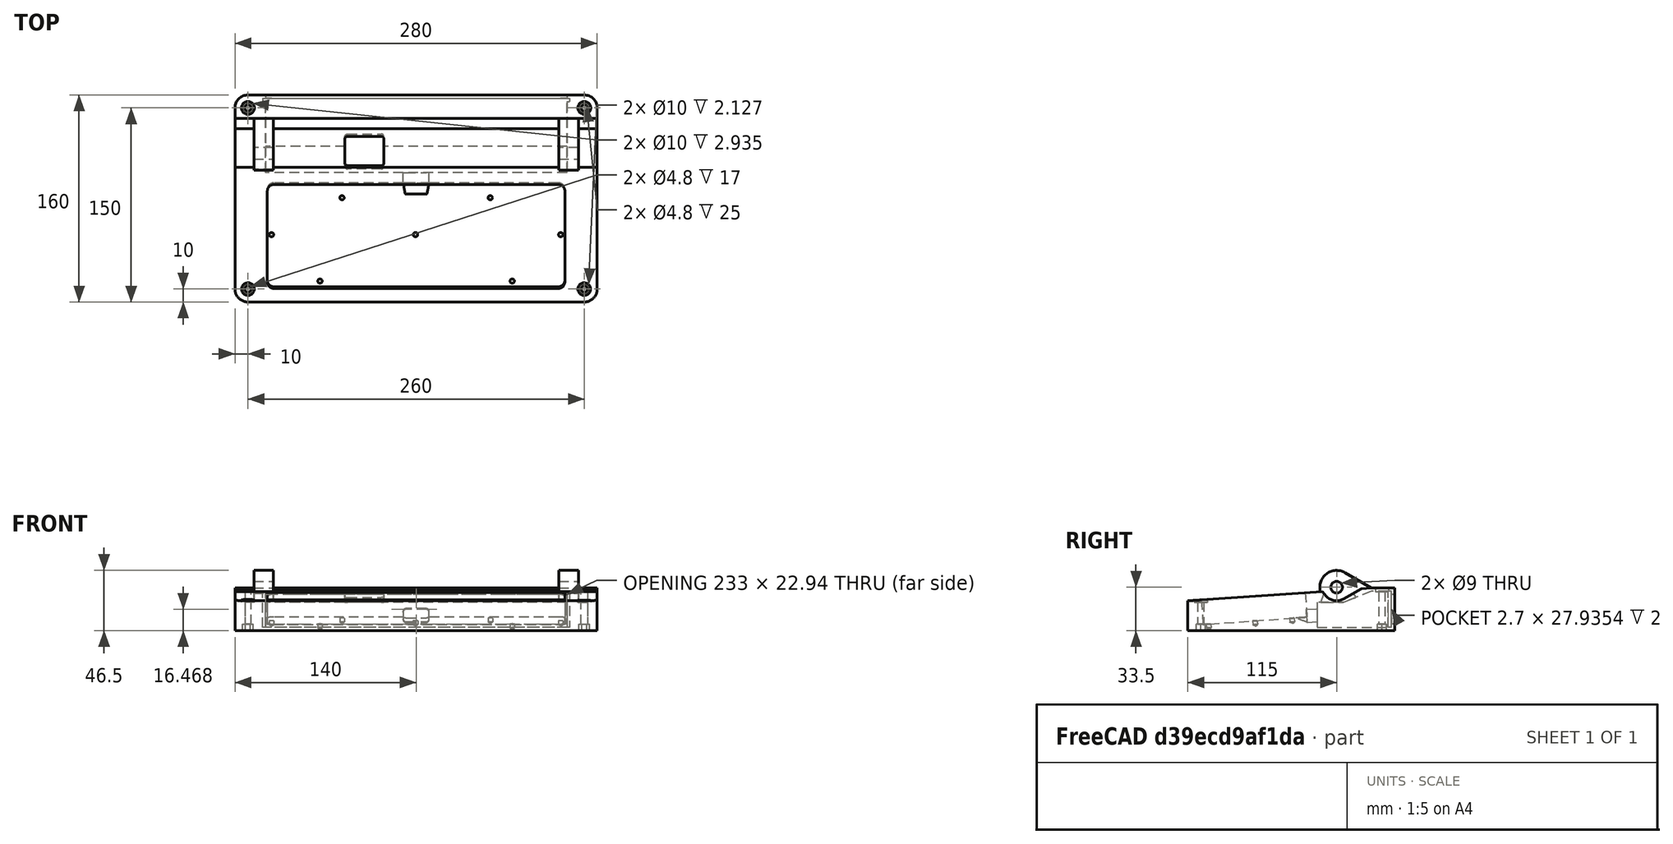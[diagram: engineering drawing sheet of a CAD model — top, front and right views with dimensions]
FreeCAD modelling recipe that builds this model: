
FCSTD DOCUMENT  (FreeCAD 1.0R39285 (Git))
Label: SimpleCheck
License: All rights reserved
LicenseURL: https://en.wikipedia.org/wiki/All_rights_reserved
objects: PartDesign::SubShapeBinder×2, App::Link×1, PartDesign::Boolean×1, PartDesign::Body×1
note: 5 computed .brp shape members not serialized (recipe doc carries the construction recipe); baked Part::Feature solids carry a one-line shape summary decoded from their .brp
EXTERNAL_REF file=Spec.FCStd obj=Spreadsheet
EXTERNAL_REF file=TestAsm.FCStd obj=Assembly
EXTERNAL_REF file=BottomEnclosure_base.FCStd obj=Body

FEATURE [App::Link] Link  label="Vars"
  LinkedObject = -> <external Spec.FCStd>#Spreadsheet
FEATURE [PartDesign::SubShapeBinder] Binder004  label="Top Enclosure"
  BindCopyOnChange = 0
  BindMode = 0
  ClaimChildren = false
  Fuse = false
  MakeFace = true
  OffsetFill = false
  OffsetIntersection = false
  OffsetJoinType = 0
  OffsetOpenResult = false
  PartialLoad = false
  Placement = pos=(0,15,33.5) rot=(1,0,0;1.0472rad)
  Refine = true
  Relative = true
  Support = -> [<external TestAsm.FCStd>#Assembly]
  _Version = 2
  expr: .Placement.Base.z = <<Vars>>.bottom_enclosure_depth + 2.5 + 1
FEATURE [PartDesign::SubShapeBinder] Binder
  BindCopyOnChange = 0
  BindMode = 0
  ClaimChildren = false
  Fuse = false
  MakeFace = true
  OffsetFill = false
  OffsetIntersection = false
  OffsetJoinType = 0
  OffsetOpenResult = false
  PartialLoad = false
  Refine = true
  Relative = true
  Support = -> [<external BottomEnclosure_base.FCStd>#Body]
  _Version = 2
FEATURE [PartDesign::Boolean] Boolean
  Group = -> [Binder]
  Refine = true
  Suppressed = false
  Type = 0
  UsePlacement = true
FEATURE [PartDesign::Body] Body
  AllowCompound = false
  Group = -> [Boolean]
  Origin = -> Origin
  Tip = -> Boolean
